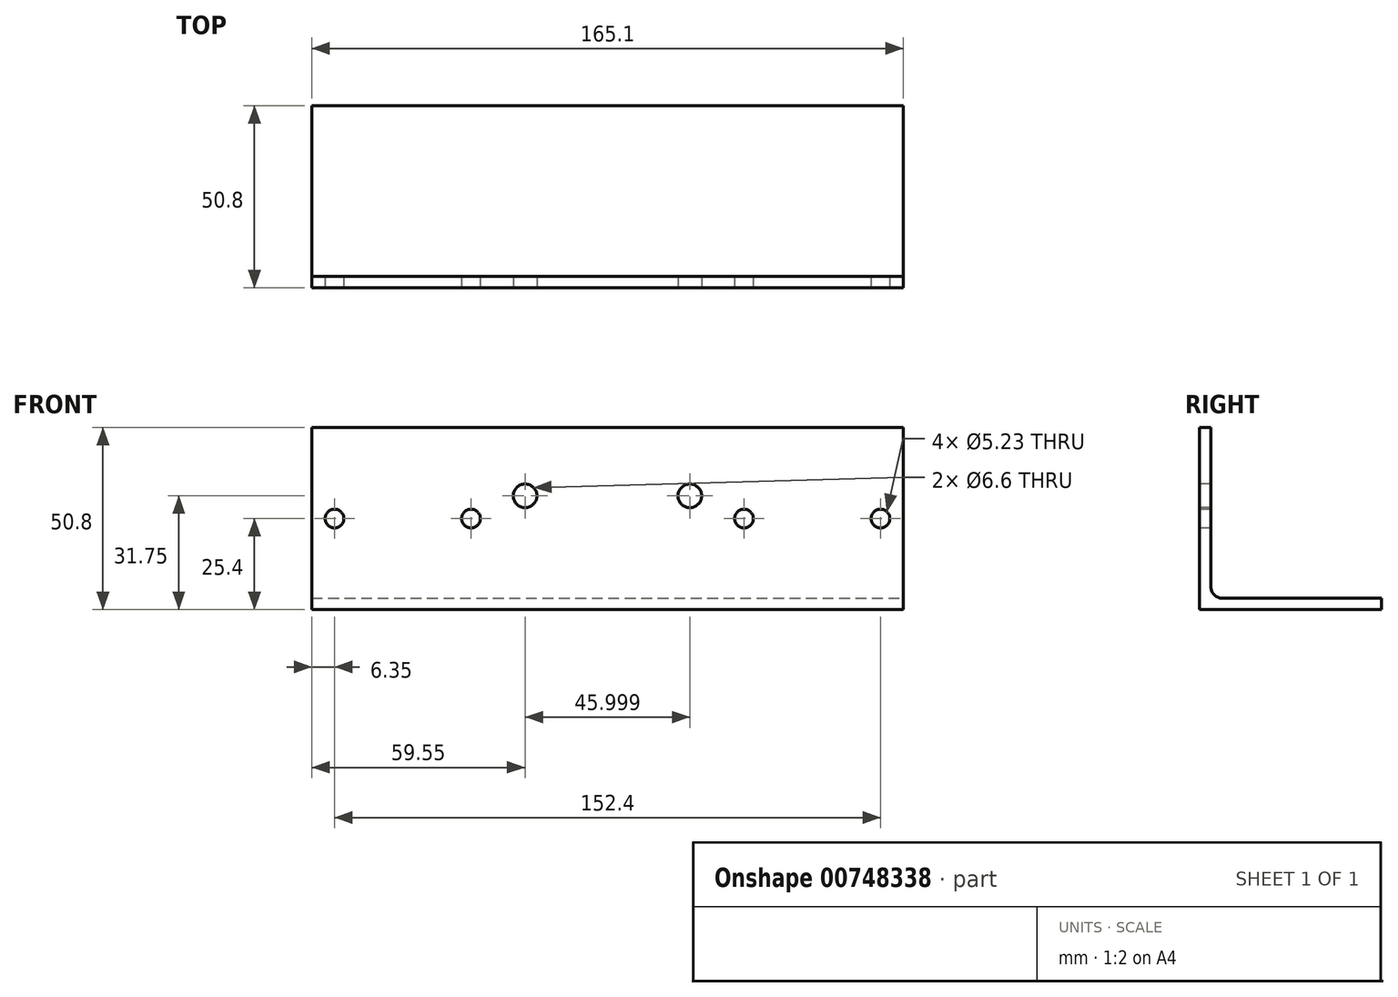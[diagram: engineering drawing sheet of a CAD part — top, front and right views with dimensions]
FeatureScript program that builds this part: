
annotation { "Feature Type Name" : "Feature", "Feature Type Description" : "" }
export const myFeature = defineFeature(function(context is Context, id is Id, definition is map)
    precondition{}
    {
        {
            var Q0;
            Q0=qCreatedBy(makeId("Right.planeOp"),FACE);
            var sketch = newSketch(context, id + "F0", { "sketchPlane" : qUnion([Q0])});
            skLineSegment(sketch, "E0", {"start": v(0, 0) * mm, "end": v(0, -44.45) * mm});
            skLineSegment(sketch, "E1", {"start": v(3.18, -47.63) * mm, "end": v(47.63, -47.62) * mm});
            skLineSegment(sketch, "E2.0", {"start": v(-3.17, -50.8) * mm, "end": v(47.63, -50.8) * mm});
            skLineSegment(sketch, "E2.1", {"start": v(-3.18, 0) * mm, "end": v(-3.17, -50.8) * mm});
            skLineSegment(sketch, "E3", {"start": v(-3.18, 0) * mm, "end": v(0, 0) * mm});
            skLineSegment(sketch, "E4", {"start": v(47.63, -47.62) * mm, "end": v(47.63, -50.8) * mm});
            skPoint(sketch, "E5.visualSharp", {"position": v(0, -47.63) * mm});
            skArc(sketch, "E5.filletArc", {"start": v(0, -44.45) * mm, "mid": v(0.93, -46.7) * mm, "end": v(3.18, -47.63) * mm});
            skSolve(sketch);
        }
        {
            var Q0;
            Q0=makeQuery(id+"F0.imprint","IMPRINT",FACE,{"disambiguationData":[TD([[makeQuery(id+"F0.imprint","IMPRINT",EDGE,{"derivedFrom":sQuery(id+"F0.wireOp",EDGE,"E0")}),-1.0]])]});
            extrude(context, id + "F1", {"entities" : qUnion([Q0]), "oppositeDirection" : true, "depth" : 165.1 * mm, "offsetDistance" : 25.4 * mm});
        }
        {
            var Q0;
            Q0=makeQuery(id+"F1.opExtrude","SWEPT_FACE",FACE,{"disambiguationData":[OSD([sQuery(id+"F0.wireOp",EDGE,"E2.1")])]});
            var sketch = newSketch(context, id + "F2", { "sketchPlane" : qUnion([Q0])});
            skLineSegment(sketch, "E6", {"start": v(-82.55, 0) * mm, "end": v(-82.55, -50.8) * mm, "construction": true});
            skLineSegment(sketch, "E7", {"start": v(0, -25.4) * mm, "end": v(-165.1, -25.4) * mm, "construction": true});
            skLineSegment(sketch, "E8", {"start": v(-25.4, 0) * mm, "end": v(-25.4, -50.8) * mm, "construction": true});
            skLineSegment(sketch, "E9", {"start": v(-139.7, 0) * mm, "end": v(-139.7, -50.8) * mm, "construction": true});
            skLineSegment(sketch, "E10.0", {"start": v(-158.75, 0) * mm, "end": v(-158.75, -50.8) * mm, "construction": true});
            skLineSegment(sketch, "E11.0", {"start": v(-120.65, 0) * mm, "end": v(-120.65, -50.8) * mm, "construction": true});
            skLineSegment(sketch, "E12.0", {"start": v(-44.45, 0) * mm, "end": v(-44.45, -50.8) * mm, "construction": true});
            skLineSegment(sketch, "E13.0", {"start": v(-6.35, 0) * mm, "end": v(-6.35, -50.8) * mm, "construction": true});
            skCircle(sketch, "E14", {"center": v(-158.75, -25.4) * mm, "radius": 2.62 * mm});
            skCircle(sketch, "E15", {"center": v(-120.65, -25.4) * mm, "radius": 2.62 * mm});
            skCircle(sketch, "E16", {"center": v(-44.45, -25.4) * mm, "radius": 2.62 * mm});
            skCircle(sketch, "E17", {"center": v(-6.35, -25.4) * mm, "radius": 2.62 * mm});
            skLineSegment(sketch, "E18.0", {"start": v(-105.55, 0) * mm, "end": v(-105.55, -50.8) * mm, "construction": true});
            skLineSegment(sketch, "E19.0", {"start": v(-59.55, 0) * mm, "end": v(-59.55, -50.8) * mm, "construction": true});
            skCircle(sketch, "E20", {"center": v(-105.55, -19.05) * mm, "radius": 3.3 * mm});
            skCircle(sketch, "E21", {"center": v(-59.55, -19.05) * mm, "radius": 3.3 * mm});
            skLineSegment(sketch, "E22.0", {"start": v(0, -19.05) * mm, "end": v(-165.1, -19.05) * mm, "construction": true});
            skSolve(sketch);
        }
        {
            var Q0;
            Q0=qSketchRegion(id+"F2",true);
            extrude(context, id + "F3", {"entities" : qUnion([Q0]), "operationType" : NewBodyOperationType.REMOVE, "endBound" : BoundingType.THROUGH_ALL, "oppositeDirection" : true, "depth" : 25.4 * mm, "offsetDistance" : 25.4 * mm});
        }
    });
